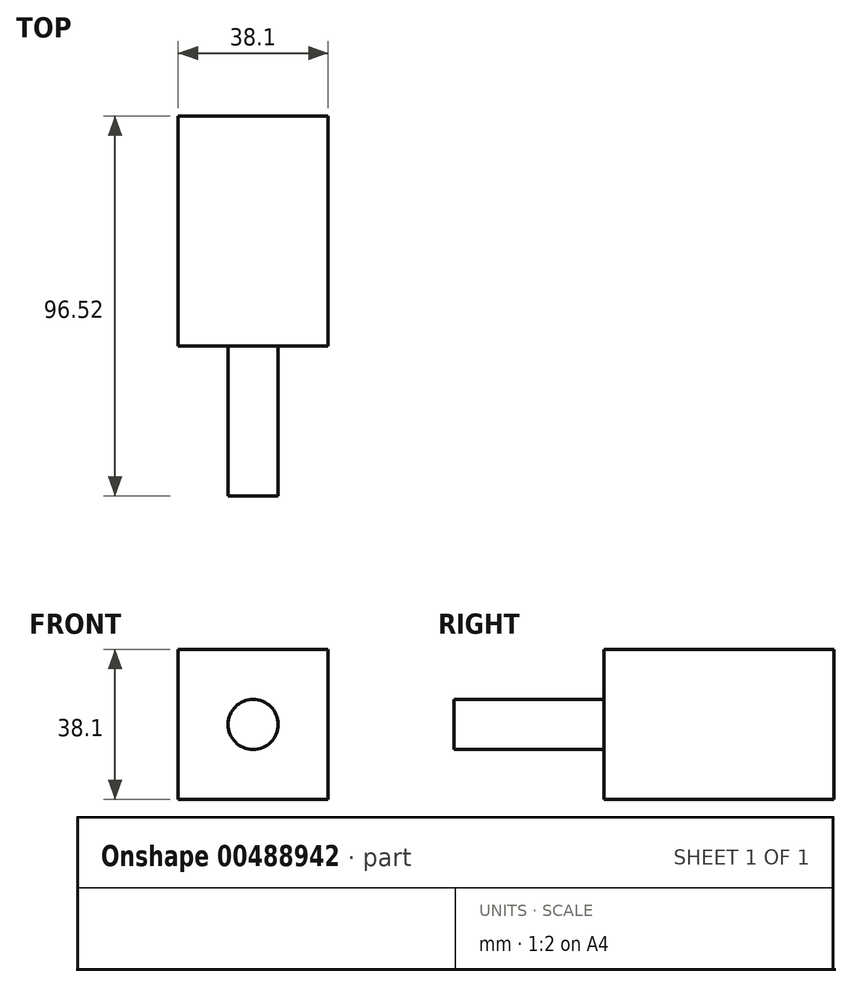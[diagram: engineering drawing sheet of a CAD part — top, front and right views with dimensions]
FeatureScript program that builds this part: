
annotation { "Feature Type Name" : "Feature", "Feature Type Description" : "" }
export const myFeature = defineFeature(function(context is Context, id is Id, definition is map)
    precondition{}
    {
        {
            var Q0;
            Q0=qCreatedBy(makeId("Top.planeOp"),FACE);
            var sketch = newSketch(context, id + "F0", { "sketchPlane" : qUnion([Q0])});
            skLineSegment(sketch, "E0.bottom", {"start": v(0, 0) * mm, "end": v(38.1, 0) * mm});
            skLineSegment(sketch, "E0.top", {"start": v(0, 58.42) * mm, "end": v(38.1, 58.42) * mm});
            skLineSegment(sketch, "E0.left", {"start": v(0, 0) * mm, "end": v(0, 58.42) * mm});
            skLineSegment(sketch, "E0.right", {"start": v(38.1, 0) * mm, "end": v(38.1, 58.42) * mm});
            skSolve(sketch);
        }
        {
            var Q0;
            Q0 = qSketchRegion(id + "F0", true);
            extrude(context, id + "F1", {"entities" : qUnion([Q0]), "depth" : 38.1 * mm});
        }
        {
            var Q0;
            Q0=makeQuery(id+"F1.opExtrude","SWEPT_FACE",FACE,{"disambiguationData":[OSD([sQuery(id+"F0.wireOp",EDGE,"E0.bottom")])]});
            var sketch = newSketch(context, id + "F2", { "sketchPlane" : qUnion([Q0])});
            skCircle(sketch, "E1", {"center": v(19.05, 19.05) * mm, "radius": 6.35 * mm});
            skPoint(sketch, "E2", {"position": v(19.05, 0) * mm});
            skPoint(sketch, "E3", {"position": v(38.1, 19.05) * mm});
            skSolve(sketch);
        }
        {
            var Q0;
            Q0 = qSketchRegion(id + "F2", true);
            extrude(context, id + "F3", {"entities" : qUnion([Q0]), "operationType" : NewBodyOperationType.ADD, "depth" : 38.1 * mm});
        }
    });
